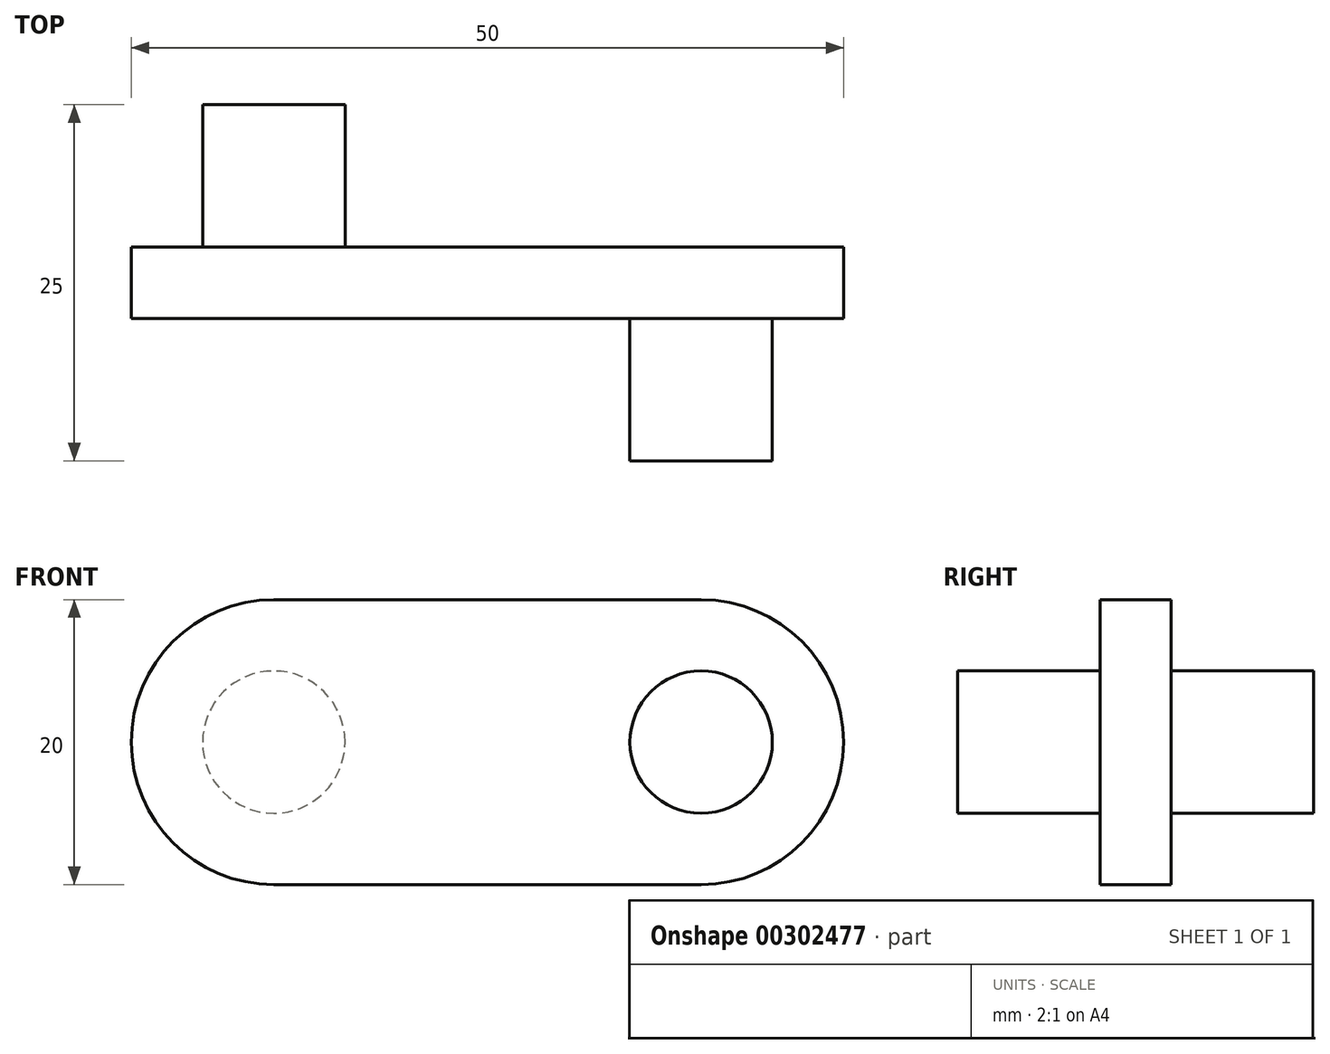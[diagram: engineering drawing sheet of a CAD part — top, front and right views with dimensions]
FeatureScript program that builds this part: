
annotation { "Feature Type Name" : "Feature", "Feature Type Description" : "" }
export const myFeature = defineFeature(function(context is Context, id is Id, definition is map)
    precondition{}
    {
        {
            var Q0;
            Q0=qCreatedBy(makeId("Front.planeOp"),FACE);
            var sketch = newSketch(context, id + "F0", { "sketchPlane" : qUnion([Q0])});
            skLineSegment(sketch, "E0", {"start": v(0, 0) * mm, "end": v(30, 0) * mm, "construction": true});
            skCircle(sketch, "E1", {"center": v(0, 0) * mm, "radius": 5 * mm});
            skCircle(sketch, "E2", {"center": v(30, 0) * mm, "radius": 5 * mm});
            skArc(sketch, "E3.0.startCap", {"start": v(0, -10) * mm, "mid": v(-10, 0) * mm, "end": v(0, 10) * mm});
            skArc(sketch, "E3.0.endCap", {"start": v(30, 10) * mm, "mid": v(40, 0) * mm, "end": v(30, -10) * mm});
            skLineSegment(sketch, "E3.0.left", {"start": v(0, 10) * mm, "end": v(30, 10) * mm});
            skLineSegment(sketch, "E3.0.right", {"start": v(0, -10) * mm, "end": v(30, -10) * mm});
            skSolve(sketch);
        }
        {
            var Q0;
            Q0=makeQuery(id+"F0.imprint","IMPRINT",FACE,{"disambiguationData":[TD([[makeQuery(id+"F0.imprint","IMPRINT",EDGE,{"derivedFrom":sQuery(id+"F0.wireOp",EDGE,"E1")}),-1.0]])]});
            extrude(context, id + "F1", {"entities" : qUnion([Q0]), "depth" : 5 * mm});
        }
        {
            var Q0;
            Q0=makeQuery(id+"F0.imprint","IMPRINT",FACE,{"disambiguationData":[TD([[makeQuery(id+"F0.imprint","IMPRINT",EDGE,{"derivedFrom":sQuery(id+"F0.wireOp",EDGE,"E2")}),1.0]])]});
            extrude(context, id + "F2", {"entities" : qUnion([Q0]), "operationType" : NewBodyOperationType.ADD, "depth" : 15 * mm});
        }
        {
            var Q0;
            Q0=makeQuery(id+"F0.imprint","IMPRINT",FACE,{"disambiguationData":[TD([[makeQuery(id+"F0.imprint","IMPRINT",EDGE,{"derivedFrom":sQuery(id+"F0.wireOp",EDGE,"E1")}),1.0]])]});
            extrude(context, id + "F3", {"entities" : qUnion([Q0]), "operationType" : NewBodyOperationType.ADD, "oppositeDirection" : true, "depth" : 10 * mm, "hasSecondDirection" : true, "secondDirectionOppositeDirection" : false, "secondDirectionDepth" : 5 * mm});
        }
    });
